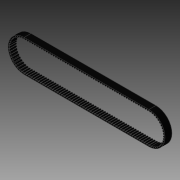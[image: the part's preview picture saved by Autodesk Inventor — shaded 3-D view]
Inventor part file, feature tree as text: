
AUTODESK INVENTOR PART (.ipt)
format: ipt  version: 2014 SP1 (Build 180222100, 222)  size: 1,411,072 bytes
history: native  units: in
note: dims shown in document units (in); Inventor stores cm internally (conversion verified against a paired STEP export)
features: extrude x2, sketch x1, pattern_linear x1
ambient origin geometry x8: Origin, YZ Plane, XZ Plane, XY Plane, X Axis, Y Axis, Z Axis, Center Point
bodies: Solid1 (feature_tree)
feature tree (4):
  sketch  "Sketch1"  dims[d0=1.29in d1=10.5507in d2=1.3315in d3=0.5906in d4=0.0in d6=58.2677in d8=0.0039in d9=0.0681in d10=0.5906in d11=0.0in]
  extrude  "Extrusion1"  Depth=10.5507in
  pattern_linear  "Rectangular Pattern1"  Spacing1=1.3315in  [1 undecoded]
  extrude  "Extrusion2"  Depth=0.5906in TaperAngle=0.0deg
note: 1 required parameter value undecoded (feature->parameter linkage not recoverable at this tier; creation-order binding heuristic only, values carry confidence <= 0.55)
